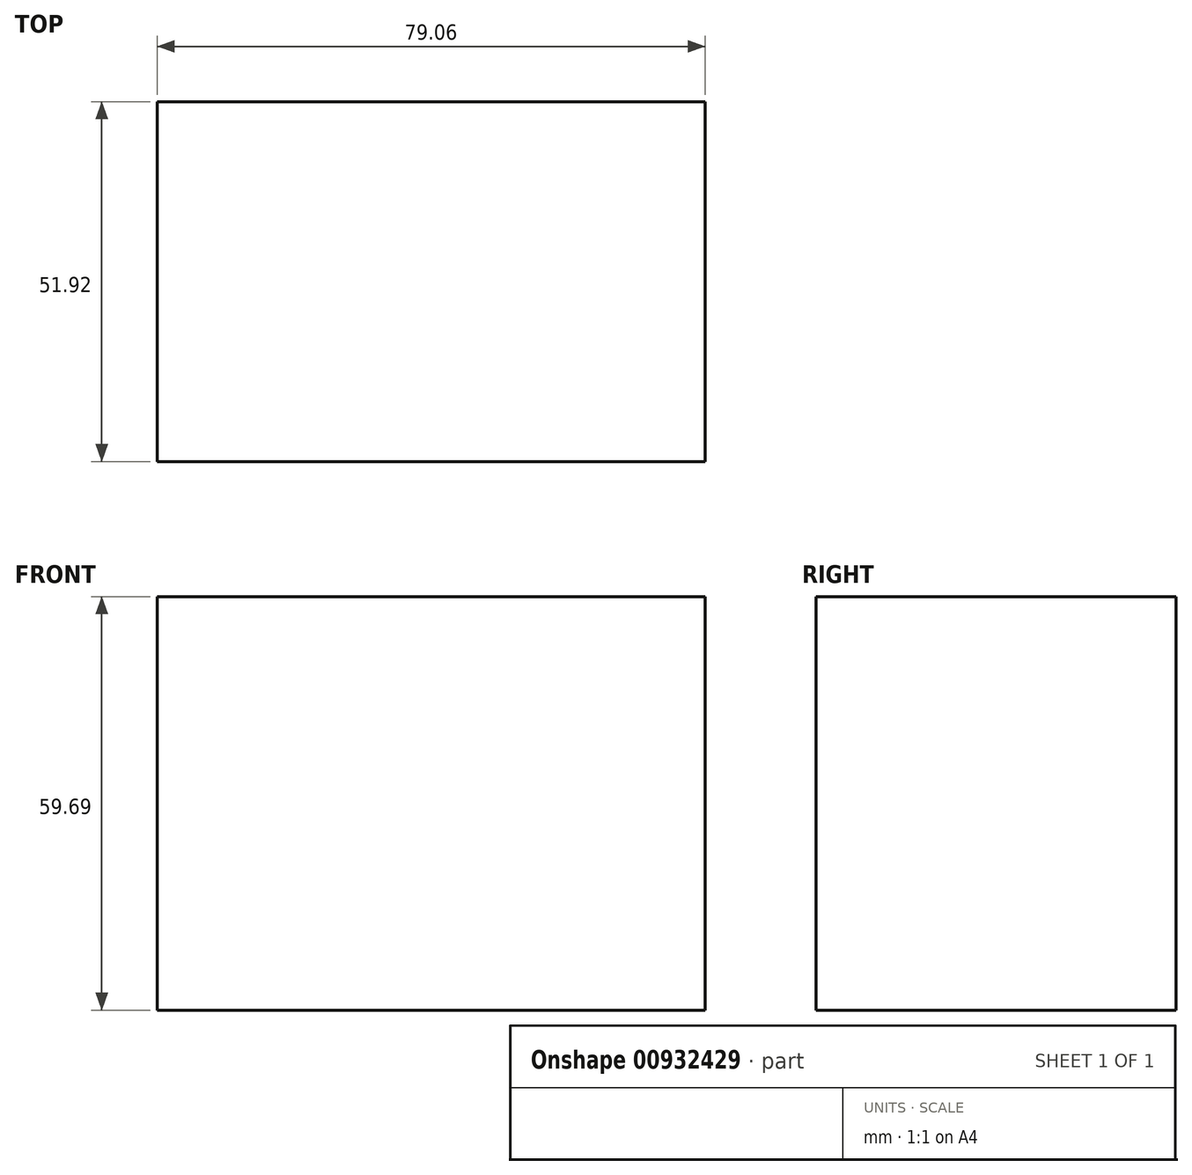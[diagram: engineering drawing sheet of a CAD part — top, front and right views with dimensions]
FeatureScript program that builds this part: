
annotation { "Feature Type Name" : "Feature", "Feature Type Description" : "" }
export const myFeature = defineFeature(function(context is Context, id is Id, definition is map)
    precondition{}
    {
        {
            var Q0;
            Q0=qCreatedBy(makeId("Top.planeOp"),FACE);
            var sketch = newSketch(context, id + "F0", { "sketchPlane" : qUnion([Q0])});
            skLineSegment(sketch, "E0.bottom", {"start": v(-58.3, 42.5) * mm, "end": v(20.77, 42.5) * mm});
            skLineSegment(sketch, "E0.top", {"start": v(-58.3, -9.42) * mm, "end": v(20.77, -9.42) * mm});
            skLineSegment(sketch, "E0.left", {"start": v(-58.3, 42.5) * mm, "end": v(-58.3, -9.42) * mm});
            skLineSegment(sketch, "E0.right", {"start": v(20.77, 42.5) * mm, "end": v(20.77, -9.42) * mm});
            skSolve(sketch);
        }
        {
            var Q0;
            Q0=makeQuery(id+"F0.imprint","IMPRINT",FACE,{"disambiguationData":[TD([[makeQuery(id+"F0.imprint","IMPRINT",EDGE,{"derivedFrom":sQuery(id+"F0.wireOp",EDGE,"E0.bottom")}),-1.0]])]});
            extrude(context, id + "F1", {"entities" : qUnion([Q0]), "depth" : 59.69 * mm, "offsetDistance" : 25.4 * mm});
        }
        {
            var Q0;
            Q0=qCreatedBy(makeId("Top.planeOp"),FACE);
            var sketch = newSketch(context, id + "F2", { "sketchPlane" : qUnion([Q0])});
            skLineSegment(sketch, "E1.bottom", {"start": v(-49.32, 33.22) * mm, "end": v(9.8, 33.22) * mm});
            skLineSegment(sketch, "E1.top", {"start": v(-49.32, 0) * mm, "end": v(9.8, 0) * mm});
            skLineSegment(sketch, "E1.left", {"start": v(-49.32, 33.22) * mm, "end": v(-49.32, 0) * mm});
            skLineSegment(sketch, "E1.right", {"start": v(9.8, 33.22) * mm, "end": v(9.8, 0) * mm});
            skSolve(sketch);
        }
        {
            var Q0;
            Q0 = qSketchRegion(id + "F2", true);
            extrude(context, id + "F3", {"entities" : qUnion([Q0]), "operationType" : NewBodyOperationType.REMOVE, "oppositeDirection" : true, "depth" : 25.4 * mm, "offsetDistance" : 25.4 * mm});
        }
    });
